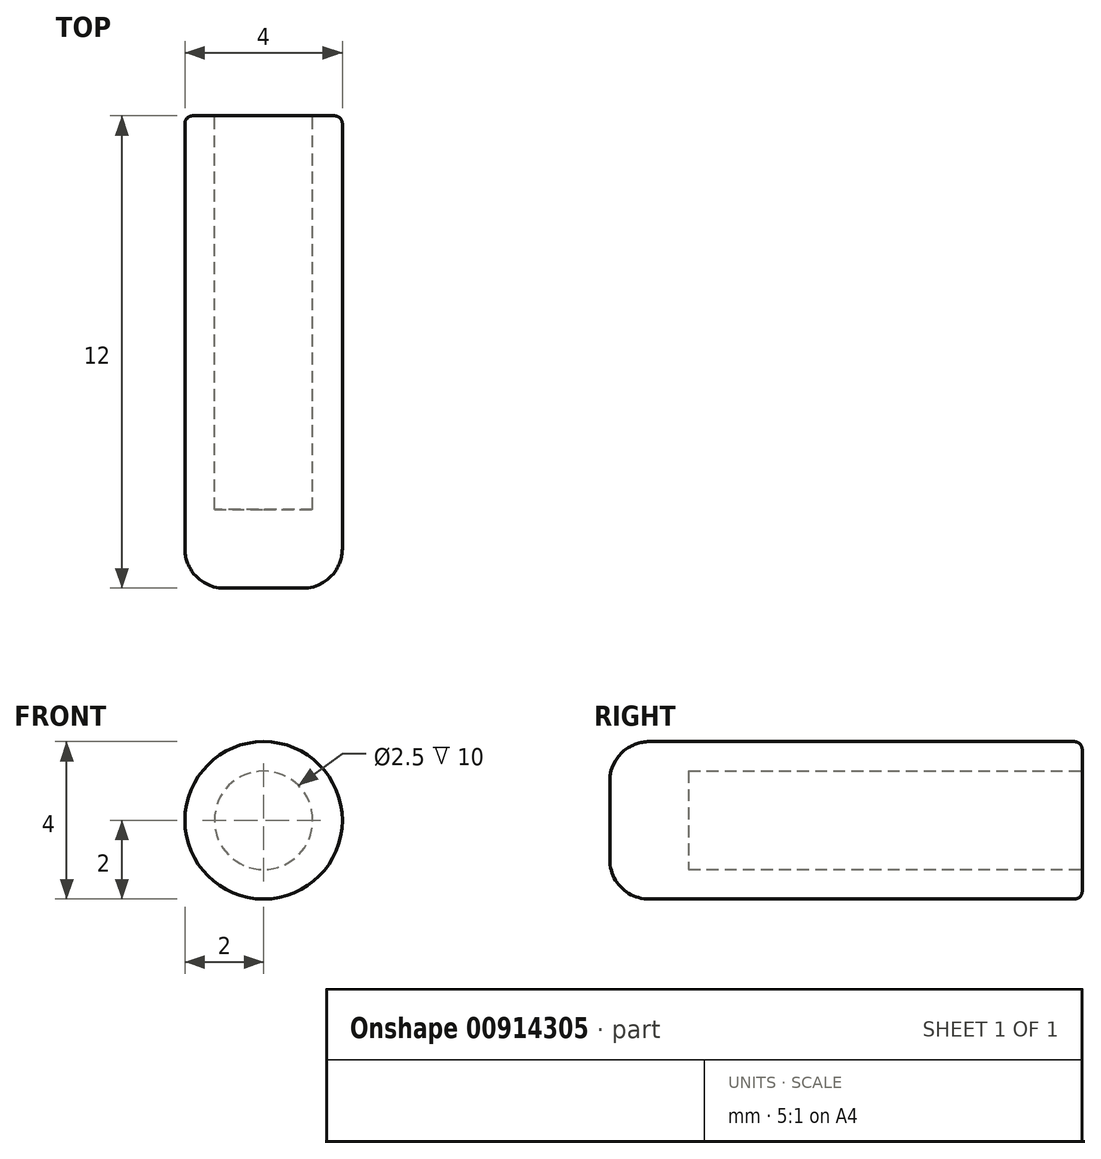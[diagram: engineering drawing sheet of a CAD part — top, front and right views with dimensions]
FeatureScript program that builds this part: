
annotation { "Feature Type Name" : "Feature", "Feature Type Description" : "" }
export const myFeature = defineFeature(function(context is Context, id is Id, definition is map)
    precondition{}
    {
        {
            assignVariable(context, id + "F0", {"name" : "length", "anyValue" : 12});
        }
        {
            var Q0;
            Q0=qCreatedBy(makeId("Front.planeOp"),FACE);
            var sketch = newSketch(context, id + "F1", { "sketchPlane" : qUnion([Q0])});
            skCircle(sketch, "E0", {"center": v(0, 0) * mm, "radius": 2 * mm});
            skSolve(sketch);
        }
        {
            var Q0;
            Q0 = qSketchRegion(id + "F1", true);
            extrude(context, id + "F2", {"entities" : qUnion([Q0]), "depth" : (getVariable(context, 'length')) * mm, "offsetDistance" : 25 * mm});
        }
        {
            var Q0;
            Q0=makeQuery(id+"F2.opExtrude","CAP_EDGE",EDGE,{"disambiguationData":[OSD([sQuery(id+"F1.wireOp",EDGE,"E0")])],"isStart":false});
            fillet(context, id + "F3", {"entities" : qUnion([Q0]), "radius" : 1 * mm, "tangentPropagation" : true, "allowEdgeOverflow" : false});
        }
        {
            var Q0;
            Q0=makeQuery(id+"F2.opExtrude","CAP_EDGE",EDGE,{"disambiguationData":[OSD([sQuery(id+"F1.wireOp",EDGE,"E0")])],"isStart":true});
            fillet(context, id + "F4", {"entities" : qUnion([Q0]), "radius" : 0.2 * mm, "tangentPropagation" : true, "allowEdgeOverflow" : false});
        }
        {
            var Q0;
            Q0=makeQuery(id+"F2.opExtrude","CAP_FACE",FACE,{"disambiguationData":[OSD([sQuery(id+"F1.wireOp",EDGE,"E0")])],"isStart":true});
            var sketch = newSketch(context, id + "F5", { "sketchPlane" : qUnion([Q0])});
            skCircle(sketch, "E1", {"center": v(0, 0) * mm, "radius": 1.25 * mm});
            skSolve(sketch);
        }
        {
            var Q0;
            Q0 = qSketchRegion(id + "F5", true);
            extrude(context, id + "F6", {"entities" : qUnion([Q0]), "operationType" : NewBodyOperationType.REMOVE, "oppositeDirection" : true, "depth" : (getVariable(context, 'length') - 2) * mm, "offsetDistance" : 25 * mm});
        }
    });
